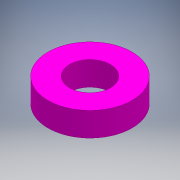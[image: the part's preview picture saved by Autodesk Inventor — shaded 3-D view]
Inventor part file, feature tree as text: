
AUTODESK INVENTOR PART (.ipt)
format: ipt  version: 2017 (Build 210142000, 142)  size: 95,232 bytes
history: native  units: mm
features: extrude x1, sketch x1
ambient origin geometry x8: Origin, YZ Plane, XZ Plane, XY Plane, X Axis, Y Axis, Z Axis, Center Point
bodies: Solid1 (feature_tree)
feature tree (2):
  extrude  "Extrusion1"  Depth=10.0mm
  sketch  "Sketch1"  dims[d0=17.0mm d1=35.0mm d2=10.0mm d3=0.0mm]
